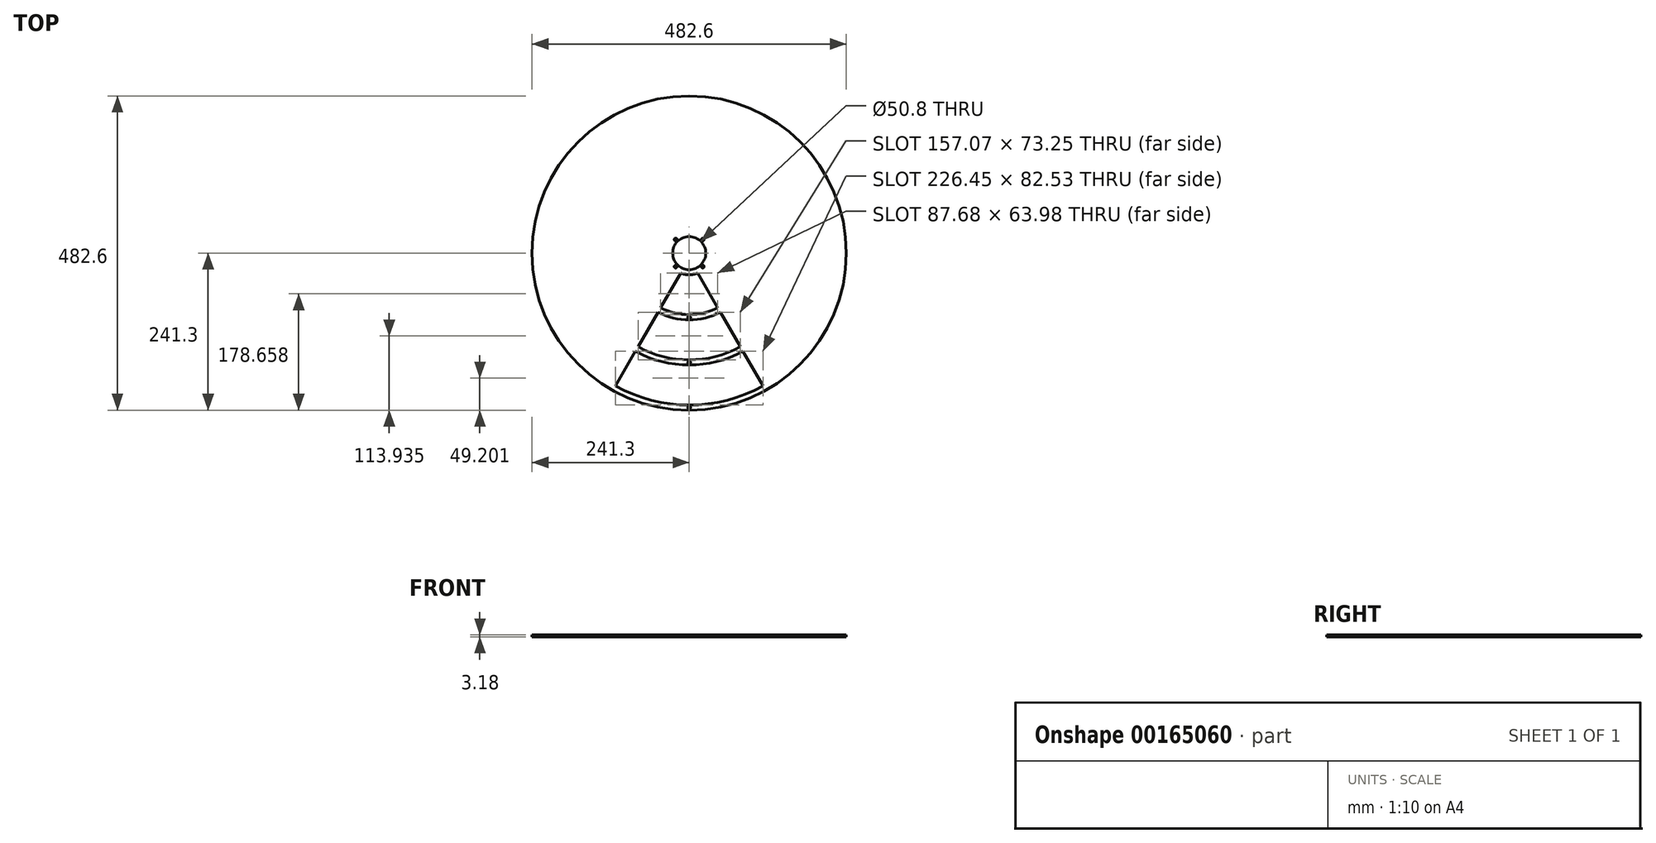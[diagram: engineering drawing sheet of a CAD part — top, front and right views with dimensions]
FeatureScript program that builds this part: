
annotation { "Feature Type Name" : "Feature", "Feature Type Description" : "" }
export const myFeature = defineFeature(function(context is Context, id is Id, definition is map)
    precondition{}
    {
        {
            var Q0;
            Q0=qCreatedBy(makeId("Top.planeOp"),FACE);
            var sketch = newSketch(context, id + "F0", { "sketchPlane" : qUnion([Q0])});
            skCircle(sketch, "E0", {"center": v(0, 0) * mm, "radius": 25.4 * mm});
            skCircle(sketch, "E1", {"center": v(0, 0) * mm, "radius": 241.3 * mm});
            skSolve(sketch);
        }
        {
            var Q0;
            Q0 = qSketchRegion(id + "F0", true);
            extrude(context, id + "F1", {"entities" : qUnion([Q0]), "depth" : 3.17 * mm});
        }
        {
            var Q0;
            Q0=makeQuery(id+"F1.opExtrude","CAP_FACE",FACE,{"disambiguationData":[OSD([sQuery(id+"F0.wireOp",EDGE,"E0"),sQuery(id+"F0.wireOp",EDGE,"E1")])],"isStart":false});
            var sketch = newSketch(context, id + "F2", { "sketchPlane" : qUnion([Q0])});
            skArc(sketch, "E2", {"start": v(-13.11, -30.65) * mm, "mid": v(0, -33.34) * mm, "end": v(13.11, -30.65) * mm});
            skArc(sketch, "E3", {"start": v(-113.23, -204.05) * mm, "mid": v(0, -233.36) * mm, "end": v(113.23, -204.05) * mm});
            skLineSegment(sketch, "E4", {"start": v(-13.11, -30.65) * mm, "end": v(-43.84, -83.87) * mm});
            skLineSegment(sketch, "E5", {"start": v(0, 0) * mm, "end": v(-31.91, -55.27) * mm, "construction": true});
            skLineSegment(sketch, "E6", {"start": v(-31.91, -55.27) * mm, "end": v(-28.48, -57.26) * mm, "construction": true});
            skLineSegment(sketch, "E7", {"start": v(0, 0) * mm, "end": v(31.91, -55.27) * mm, "construction": true});
            skLineSegment(sketch, "E8", {"start": v(31.91, -55.27) * mm, "end": v(28.48, -57.26) * mm, "construction": true});
            skLineSegment(sketch, "E9", {"start": v(0, 0) * mm, "end": v(0, -33.34) * mm, "construction": true});
            skLineSegment(sketch, "E10", {"start": v(13.11, -30.65) * mm, "end": v(43.84, -83.87) * mm});
            skArc(sketch, "E11", {"start": v(-43.84, -83.87) * mm, "mid": v(0, -94.63) * mm, "end": v(43.84, -83.87) * mm});
            skLineSegment(sketch, "E12", {"start": v(-43.84, -83.87) * mm, "end": v(-47.8, -90.74) * mm, "construction": true});
            skLineSegment(sketch, "E13", {"start": v(43.84, -83.87) * mm, "end": v(47.8, -90.74) * mm, "construction": true});
            skLineSegment(sketch, "E14", {"start": v(-47.8, -90.74) * mm, "end": v(-78.53, -143.96) * mm});
            skLineSegment(sketch, "E15", {"start": v(-78.53, -143.96) * mm, "end": v(-82.5, -150.83) * mm, "construction": true});
            skLineSegment(sketch, "E16", {"start": v(-82.5, -150.83) * mm, "end": v(-113.23, -204.05) * mm});
            skArc(sketch, "E17", {"start": v(-47.8, -90.74) * mm, "mid": v(0, -102.57) * mm, "end": v(47.8, -90.74) * mm});
            skArc(sketch, "E18", {"start": v(-78.53, -143.96) * mm, "mid": v(0, -163.99) * mm, "end": v(78.53, -143.96) * mm});
            skArc(sketch, "E19", {"start": v(-82.5, -150.83) * mm, "mid": v(0, -171.92) * mm, "end": v(82.5, -150.83) * mm});
            skLineSegment(sketch, "E20", {"start": v(47.8, -90.74) * mm, "end": v(78.53, -143.96) * mm});
            skLineSegment(sketch, "E21", {"start": v(78.53, -143.96) * mm, "end": v(82.5, -150.83) * mm, "construction": true});
            skLineSegment(sketch, "E22", {"start": v(82.5, -150.83) * mm, "end": v(113.23, -204.05) * mm});
            skLineSegment(sketch, "E23", {"start": v(0, -33.34) * mm, "end": v(0, -94.63) * mm, "construction": true});
            skLineSegment(sketch, "E24", {"start": v(0, -94.63) * mm, "end": v(0, -102.57) * mm, "construction": true});
            skLineSegment(sketch, "E25", {"start": v(0, -102.57) * mm, "end": v(0, -163.99) * mm, "construction": true});
            skLineSegment(sketch, "E26", {"start": v(0, -163.99) * mm, "end": v(0, -171.92) * mm, "construction": true});
            skLineSegment(sketch, "E27", {"start": v(0, -171.92) * mm, "end": v(0, -233.36) * mm, "construction": true});
            skLineSegment(sketch, "E28", {"start": v(0, -233.36) * mm, "end": v(0, -241.3) * mm, "construction": true});
            skCircle(sketch, "E29", {"center": v(0, -98.6) * mm, "radius": 2.15 * mm});
            skCircle(sketch, "E30", {"center": v(0, -167.96) * mm, "radius": 2.15 * mm});
            skCircle(sketch, "E31", {"center": v(0, -237.33) * mm, "radius": 2.15 * mm});
            skSolve(sketch);
        }
        {
            var Q0;
            Q0 = qSketchRegion(id + "F2", true);
            var Q1;
            Q1=makeQuery(id+"F1.opExtrude","CAP_FACE",FACE,{"disambiguationData":[OSD([sQuery(id+"F0.wireOp",EDGE,"E0"),sQuery(id+"F0.wireOp",EDGE,"E1")])],"isStart":true});
            extrude(context, id + "F3", {"entities" : qUnion([Q0]), "operationType" : NewBodyOperationType.REMOVE, "endBound" : BoundingType.UP_TO_SURFACE, "oppositeDirection" : true, "endBoundEntityFace" : qUnion([Q1]), "depth" : 25.4 * mm});
        }
        {
            var Q0;
            Q0=makeQuery(id+"F1.opExtrude","CAP_FACE",FACE,{"disambiguationData":[OSD([sQuery(id+"F0.wireOp",EDGE,"E0"),sQuery(id+"F0.wireOp",EDGE,"E1")])],"isStart":false});
            var sketch = newSketch(context, id + "F4", { "sketchPlane" : qUnion([Q0])});
            skLineSegment(sketch, "E32.bottom", {"start": v(20.77, 20.77) * mm, "end": v(-20.77, 20.77) * mm, "construction": true});
            skLineSegment(sketch, "E32.top", {"start": v(20.77, -20.77) * mm, "end": v(-20.77, -20.77) * mm, "construction": true});
            skLineSegment(sketch, "E32.left", {"start": v(-20.77, -20.77) * mm, "end": v(-20.77, 20.77) * mm, "construction": true});
            skLineSegment(sketch, "E32.right", {"start": v(20.77, -20.77) * mm, "end": v(20.77, 20.77) * mm, "construction": true});
            skPoint(sketch, "E32.middle", {"position": v(0, 0) * mm});
            skCircle(sketch, "E33", {"center": v(-20.77, 20.77) * mm, "radius": 3.97 * mm, "construction": true});
            skCircle(sketch, "E34", {"center": v(-20.77, 20.77) * mm, "radius": 2.15 * mm});
            skCircle(sketch, "E35", {"center": v(20.77, 20.77) * mm, "radius": 2.15 * mm});
            skCircle(sketch, "E36", {"center": v(20.77, -20.77) * mm, "radius": 2.15 * mm});
            skCircle(sketch, "E37", {"center": v(-20.77, -20.77) * mm, "radius": 2.15 * mm});
            skSolve(sketch);
        }
        {
            var Q0;
            Q0 = qSketchRegion(id + "F4", true);
            var Q1;
            Q1=makeQuery(id+"F1.opExtrude","CAP_FACE",FACE,{"disambiguationData":[OSD([sQuery(id+"F0.wireOp",EDGE,"E0"),sQuery(id+"F0.wireOp",EDGE,"E1")])],"isStart":true});
            extrude(context, id + "F5", {"entities" : qUnion([Q0]), "operationType" : NewBodyOperationType.REMOVE, "endBound" : BoundingType.UP_TO_SURFACE, "oppositeDirection" : true, "endBoundEntityFace" : qUnion([Q1]), "depth" : 25.4 * mm});
        }
    });
